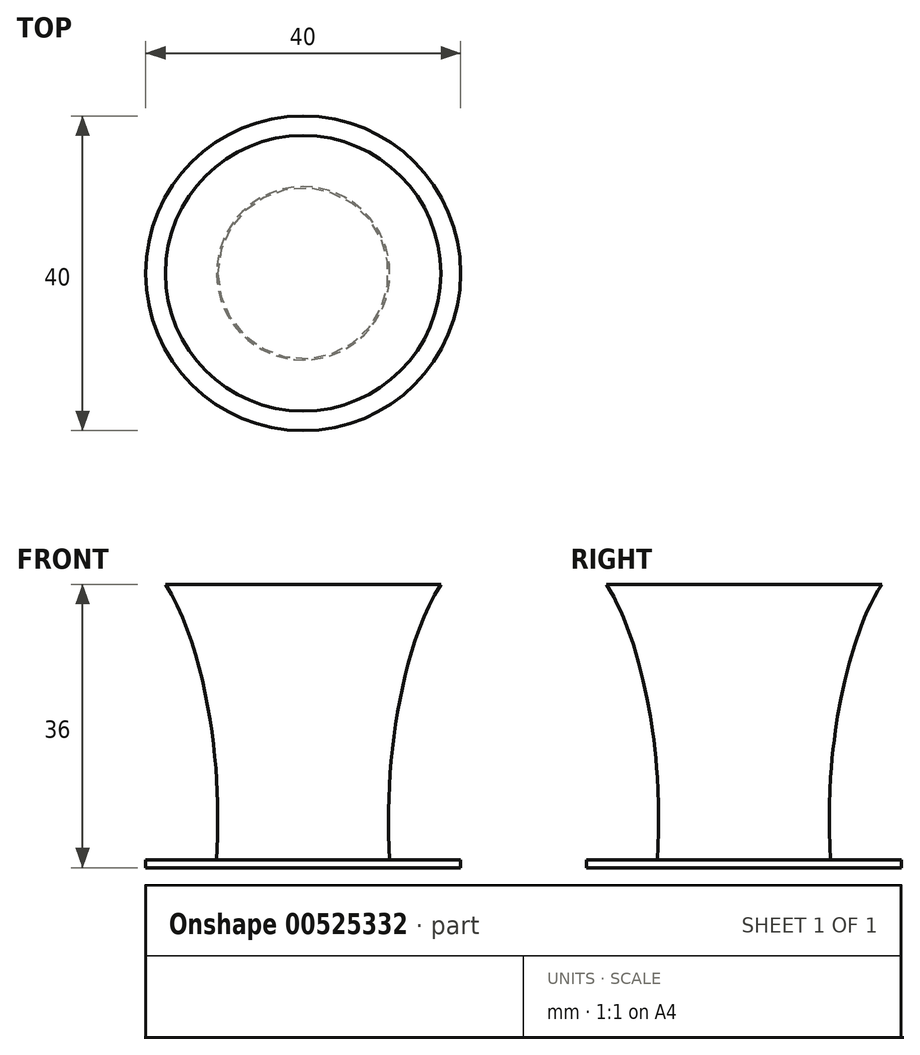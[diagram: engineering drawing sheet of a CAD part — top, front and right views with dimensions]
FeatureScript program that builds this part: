
annotation { "Feature Type Name" : "Feature", "Feature Type Description" : "" }
export const myFeature = defineFeature(function(context is Context, id is Id, definition is map)
    precondition{}
    {
        {
            var Q0;
            Q0=qCreatedBy(makeId("Top.planeOp"),FACE);
            var sketch = newSketch(context, id + "F0", { "sketchPlane" : qUnion([Q0])});
            skCircle(sketch, "E0", {"center": v(0, 0) * mm, "radius": 20 * mm});
            skSolve(sketch);
        }
        {
            var Q0;
            Q0=makeQuery(id+"F0.imprint","IMPRINT",FACE,{"disambiguationData":[TD([[makeQuery(id+"F0.imprint","IMPRINT",EDGE,{"derivedFrom":sQuery(id+"F0.wireOp",EDGE,"E0")}),1.0]])]});
            extrude(context, id + "F1", {"entities" : qUnion([Q0]), "depth" : 1 * mm, "offsetDistance" : 25 * mm});
        }
        {
            var Q0;
            Q0=qCreatedBy(makeId("Right.planeOp"),FACE);
            var sketch = newSketch(context, id + "F2", { "sketchPlane" : qUnion([Q0])});
            skLineSegment(sketch, "E1", {"start": v(0, 1) * mm, "end": v(0, 36) * mm});
            skLineSegment(sketch, "E2", {"start": v(0, 36) * mm, "end": v(17.5, 36) * mm});
            skLineSegment(sketch, "E3", {"start": v(0, 1) * mm, "end": v(11, 1) * mm});
            skFitSpline(sketch, "E4", {"points": [v(17.5, 36) * mm, v(11.57, 17.04) * mm, v(11, 1) * mm], "startDerivative": vector(-18.63, -29.3) * mm, "endDerivative": vector(1.82, -33.81) * mm});
            skSolve(sketch);
        }
        {
            var Q0;
            Q0=makeQuery(id+"F2.imprint","IMPRINT",FACE,{"disambiguationData":[TD([[makeQuery(id+"F2.imprint","IMPRINT",EDGE,{"derivedFrom":sQuery(id+"F2.wireOp",EDGE,"E1")}),-1.0]])]});
            var Q1;
            Q1=sQuery(id+"F2.wireOp",EDGE,"E1");
            revolve(context, id + "F3", {"operationType" : NewBodyOperationType.ADD, "entities" : qUnion([Q0]), "axis" : qUnion([Q1]), "revolveType" : RevolveType.FULL});
        }
    });
